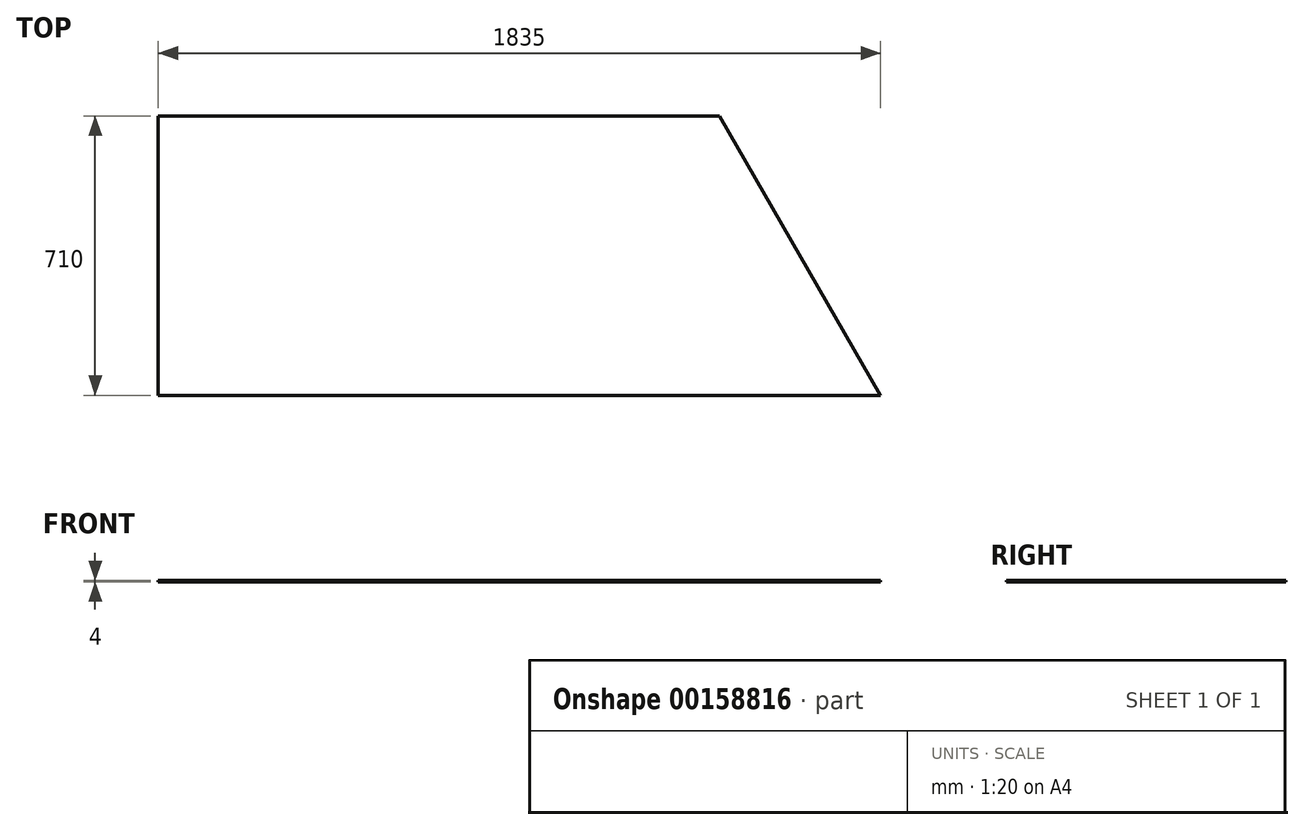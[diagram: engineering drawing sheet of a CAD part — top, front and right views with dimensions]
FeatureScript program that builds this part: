
annotation { "Feature Type Name" : "Feature", "Feature Type Description" : "" }
export const myFeature = defineFeature(function(context is Context, id is Id, definition is map)
    precondition{}
    {
        {
            var Q0;
            Q0=qCreatedBy(makeId("Top.planeOp"),FACE);
            var sketch = newSketch(context, id + "F0", { "sketchPlane" : qUnion([Q0])});
            skLineSegment(sketch, "E0", {"start": v(0, 0) * mm, "end": v(1835, 0) * mm});
            skLineSegment(sketch, "E1", {"start": v(0, 0) * mm, "end": v(0, 710) * mm});
            skLineSegment(sketch, "E2", {"start": v(0, 710) * mm, "end": v(1425, 710) * mm});
            skLineSegment(sketch, "E3", {"start": v(1425, 710) * mm, "end": v(1835, 0) * mm});
            skSolve(sketch);
        }
        {
            var Q0;
            Q0=qSketchRegion(id+"F0",true);
            extrude(context, id + "F1", {"entities" : qUnion([Q0]), "depth" : 4 * mm});
        }
    });
